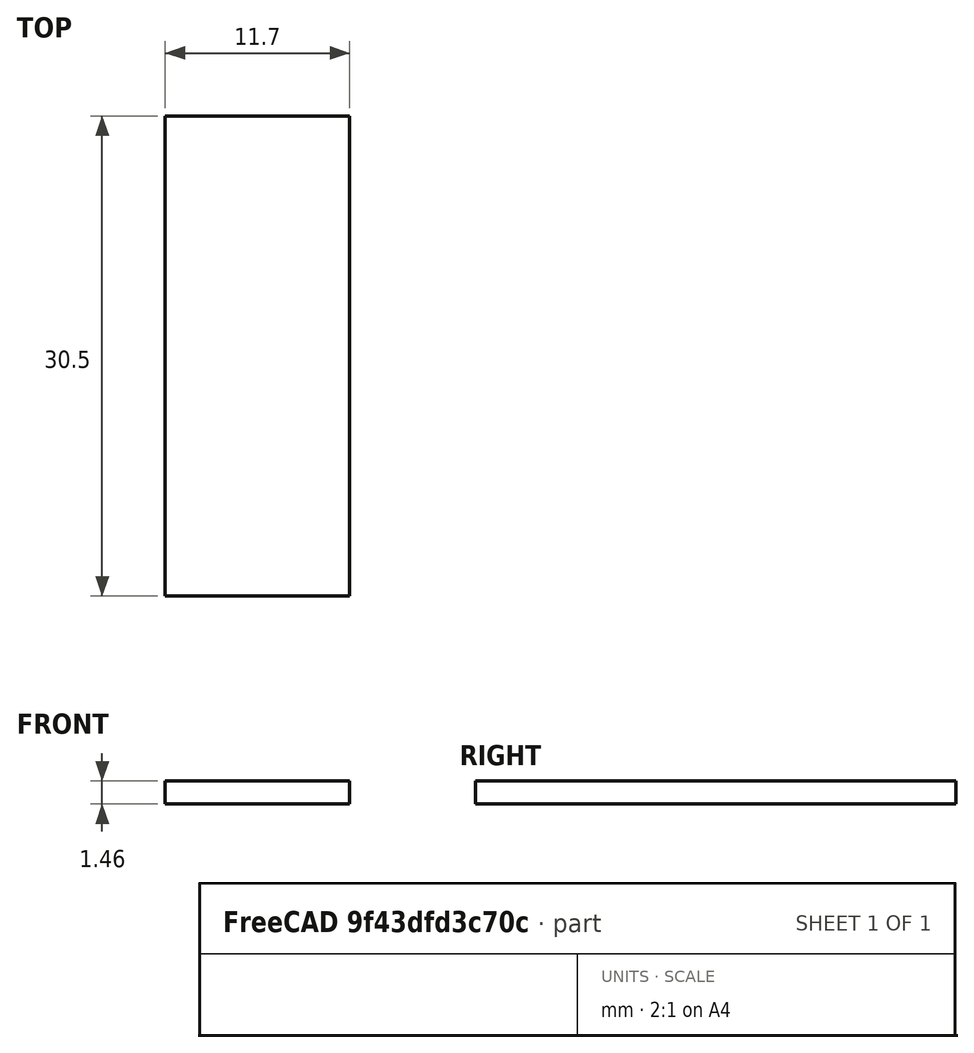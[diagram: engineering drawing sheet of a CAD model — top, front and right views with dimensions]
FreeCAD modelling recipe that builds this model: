
FCSTD DOCUMENT  (FreeCAD 0.19R24291 (Git))
Label: OLED_screen
License: All rights reserved
LicenseURL: http://en.wikipedia.org/wiki/All_rights_reserved
objects: Sketcher::SketchObject×1, PartDesign::Pad×1, PartDesign::Body×1
note: 4 computed .brp shape members not serialized (recipe doc carries the construction recipe); baked Part::Feature solids carry a one-line shape summary decoded from their .brp

FEATURE [Sketcher::SketchObject] Sketch
  FullyConstrained = false
  MapMode = 5
  Support = -> [XY_Plane]
  sketch-geometry (4):
    g0: LineSegment StartX=0 StartY=0 StartZ=0 EndX=11.6991 EndY=0 EndZ=0
    g1: LineSegment StartX=11.6991 StartY=0 StartZ=0 EndX=11.6991 EndY=-30.4986 EndZ=0
    g2: LineSegment StartX=11.6991 StartY=-30.4986 StartZ=0 EndX=0 EndY=-30.4986 EndZ=0
    g3: LineSegment StartX=0 StartY=-30.4986 StartZ=0 EndX=0 EndY=0 EndZ=0
  constraints (9):
    c: Coincident(g0,g1)
    c: Coincident(g1,g2)
    c: Coincident(g2,g3)
    c: Coincident(g3,g0)
    c: Horizontal(g0)
    c: Horizontal(g2)
    c: Vertical(g1)
    c: Vertical(g3)
    c: Coincident(g0,g-1)
FEATURE [PartDesign::Pad] Pad
  Direction = (1,1,1)
  Length = 1.46
  Length2 = 100
  Profile = -> Sketch
  Type = 0
FEATURE [PartDesign::Body] Body
  Group = -> [Sketch,Pad]
  Origin = -> Origin
  Tip = -> Pad
